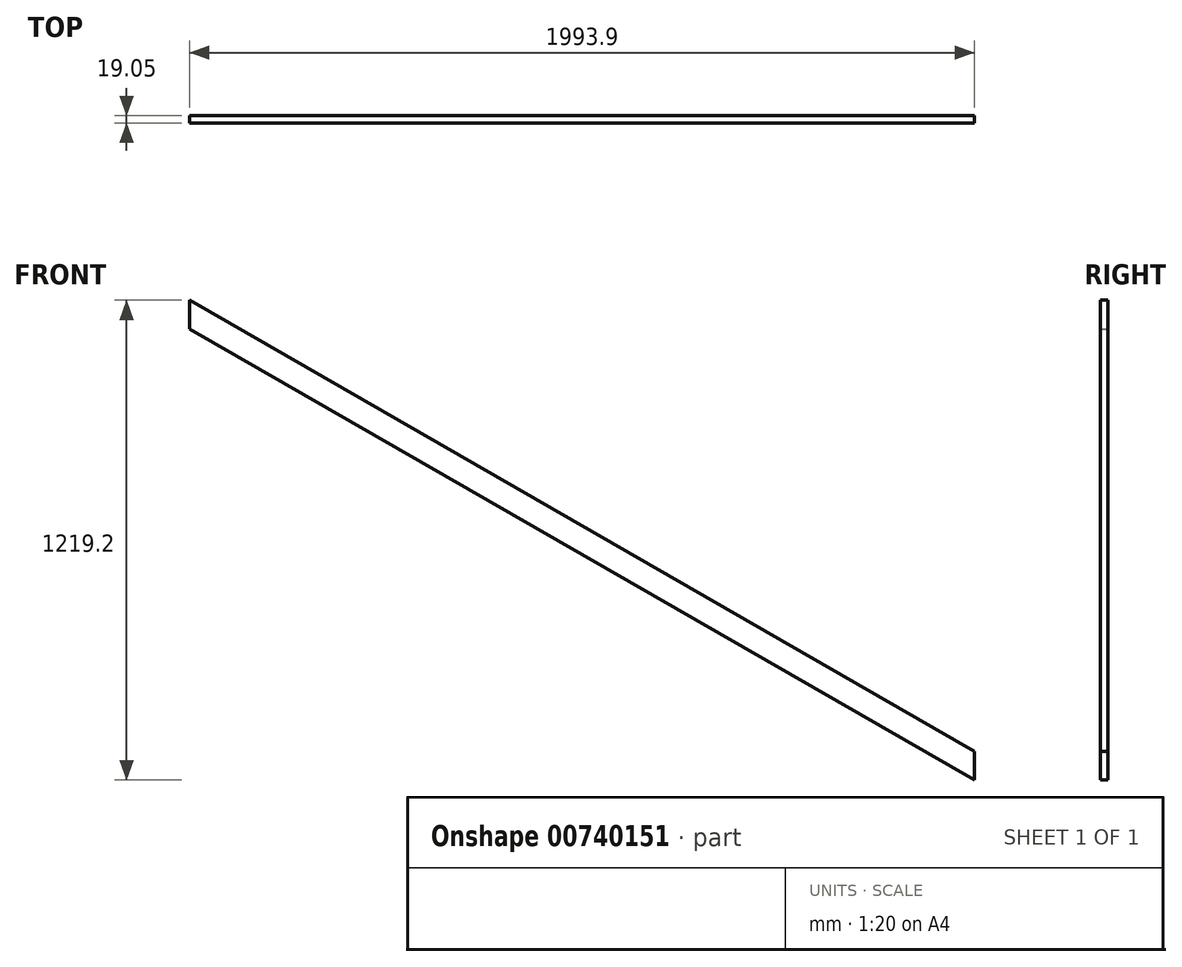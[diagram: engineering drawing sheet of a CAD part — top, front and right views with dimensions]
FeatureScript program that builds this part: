
annotation { "Feature Type Name" : "Feature", "Feature Type Description" : "" }
export const myFeature = defineFeature(function(context is Context, id is Id, definition is map)
    precondition{}
    {
        {
            var Q0;
            Q0=qCreatedBy(makeId("Front.planeOp"),FACE);
            var sketch = newSketch(context, id + "F0", { "sketchPlane" : qUnion([Q0])});
            skLineSegment(sketch, "E0.bottom", {"start": v(-799.93, 567.05) * mm, "end": v(1193.97, 567.05) * mm});
            skLineSegment(sketch, "E0.top", {"start": v(-799.93, -652.15) * mm, "end": v(1193.97, -652.15) * mm});
            skLineSegment(sketch, "E0.left", {"start": v(-799.93, 567.05) * mm, "end": v(-799.93, -652.15) * mm});
            skLineSegment(sketch, "E0.right", {"start": v(1193.97, 567.05) * mm, "end": v(1193.97, -652.15) * mm});
            skLineSegment(sketch, "E1.bottom", {"start": v(-799.93, 567.05) * mm, "end": v(1225.61, -597.1) * mm});
            skLineSegment(sketch, "E1.top", {"start": v(-831.57, 512) * mm, "end": v(1193.97, -652.15) * mm});
            skLineSegment(sketch, "E1.left", {"start": v(-799.93, 567.05) * mm, "end": v(-831.57, 512) * mm});
            skLineSegment(sketch, "E1.right", {"start": v(1225.61, -597.1) * mm, "end": v(1193.97, -652.15) * mm});
            skPoint(sketch, "E1.middle", {"position": v(197.02, -42.55) * mm});
            skPoint(sketch, "E1.middle.positionSnap0", {"position": v(197.02, 567.05) * mm});
            skPoint(sketch, "E1.middle.positionSnap1", {"position": v(-799.93, -42.55) * mm});
            skPoint(sketch, "E1.centerSnap0", {"position": v(197.02, 567.05) * mm});
            skPoint(sketch, "E1.centerSnap1", {"position": v(-799.93, -42.55) * mm});
            skSolve(sketch);
        }
        {
            var Q0;
            {var subQ1=sQuery(id+"F0.wireOp",EDGE,"E0.left");var subQ3=sQuery(id+"F0.wireOp",EDGE,"E1.top");var subQ4=makeQuery(id+"F0.imprint","INTERSECT",VERTEX,{"derivedFrom":[subQ1,subQ3]});Q0=makeQuery(id+"F0.imprint","IMPRINT",FACE,{"disambiguationData":[TD([[makeQuery(id+"F0.imprint","IMPRINT",EDGE,{"disambiguationData":[TD([[subQ4,1.0]])],"derivedFrom":subQ1}),1.0]])]});}
            extrude(context, id + "F1", {"entities" : qUnion([Q0]), "depth" : 19.05 * mm, "offsetDistance" : 25.4 * mm});
        }
    });
